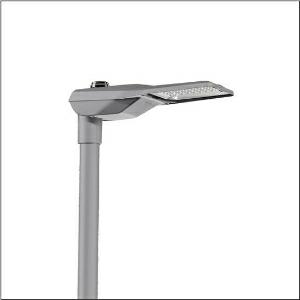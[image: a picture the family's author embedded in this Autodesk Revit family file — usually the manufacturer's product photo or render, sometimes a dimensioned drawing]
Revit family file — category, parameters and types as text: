
# Revit family: streetlight_sl_21_mini___st1_5a_5xe6p37n08gb_e583
name_source: partatom
category: Lighting Fixtures
units: mm (PartAtom-declared; Revit-internal decimal feet)

## family parameters
Cut with Voids When Loaded = No
Host = Face
Light Source = No
Part Type = Normal
Room Calculation Point = No
Round Connector Dimension = Use Diameter
Shared = No

## types (1)
- --- (1 x LED, 5840 lm, 40.4 W, 3000K)
    Apparent Load = 40 VA
    CIE Flux Codes = 22 53 95 100 100
    Color Rendering = 70
    Color Temperature = 3000K
    Default Elevation = 1800 mm
    Description = Streetlight SL 21 mini, mast luminaire, primary light control with lens, of PMMA, primary optical cover: cover, of toughened safety glass, transparent, light distribution: ST1.5a, light emission: direct distribution, primary light characteristic: asymmetric, installation type: side-entry, LED, 3G 1.5mm², High Power LED, rated luminous flux: 5.840lm, luminous efficacy: 145lm/W, light colour: 730, colour temperature: 3000K, control gear: NEMA (7pin), control: overheat protection, pre-setting: linear dimming characteristic, constant luminous flux control, time-dependent luminous flux control, flexible luminous flux parameterisation, mains connection: 230..240V, AC, 50/60Hz, connection cable pre-assembled, cable length: 8,5m, wiring characteristics: H07RN-F, start of lifetime: 40W, end of service life: 41W, reduction: 19W, luminaire housing, of diecast aluminium (EN AC-44300), powder-coated, SITECO metallic grey (DB 702S), corrosivity category C5 high according to DIN EN ISO 12944, multi-level sealing system, sealing non-destructively replaceable, inclination adjustable: 0°, 5°, 10°, 15°, length: 628mm, width: 235mm, height: 110mm, spigot size: 42mm (side-entry), mounting height: 4..8m, protection rating (complete): IP66, insulation class (complete): insulation class I (protective earthing), certification: CE, ENEC, ENEC+, VDE, impact resistance: IK10, permissible operating ambient temperature for outdoor applications: -40..+50°C, standard-compliant lighting for roads and squares, packaging unit: 1 piece

Light Distribution: ST1.5a
    Height = 110 mm
    Lamp = 1 x LED
    Lamp Light Flux = 5840 lm
    Lamp Power = 40.4 W
    Lamp count = 1
    Length = 625 mm
    Luminous efficacy = 145 lm/W
    Manufacturer = Siteco
    ModVariant = No
    Model = 5XE6P37N08GB
    Number of Poles = 1
    OnlyDefault = Yes
    Power Factor = 1
    Product Name = Streetlight SL 21 mini | ST1.5a
    Product group = mast luminaire | pylon top
    ProductGroupID = 6100
    Protection Class = Protection class I
    Protection Degree = IP 66
    RLX_Detail_Level = 1
    RLX_Emergency_Light_Flux = 0 lm
    RLX_Emergency_Type = 0
    RLX_Emergency_Type_DB = No
    RlxData = <blob elided: 29349 chars, md5=8ae5ed08>
    Socket = socket
    Standby Power = 0 W
    System Light Flux = 5840 lm
    System Power = 40 W
    Type Comments = factory setting: luminous flux: 100 % | dim-lin: 254 | 812 mA
    Type Image = l_1294379.jpg
    URL = http://relux.com
    VarID = @adj_133153
    Voltage = 0 V
    Weight = 0.00 kg
    Width = 234 mm

## geometry (parser evidence)
native form markers: Blend x4, Sweep x9
no freeform markers — native parametric forms only
